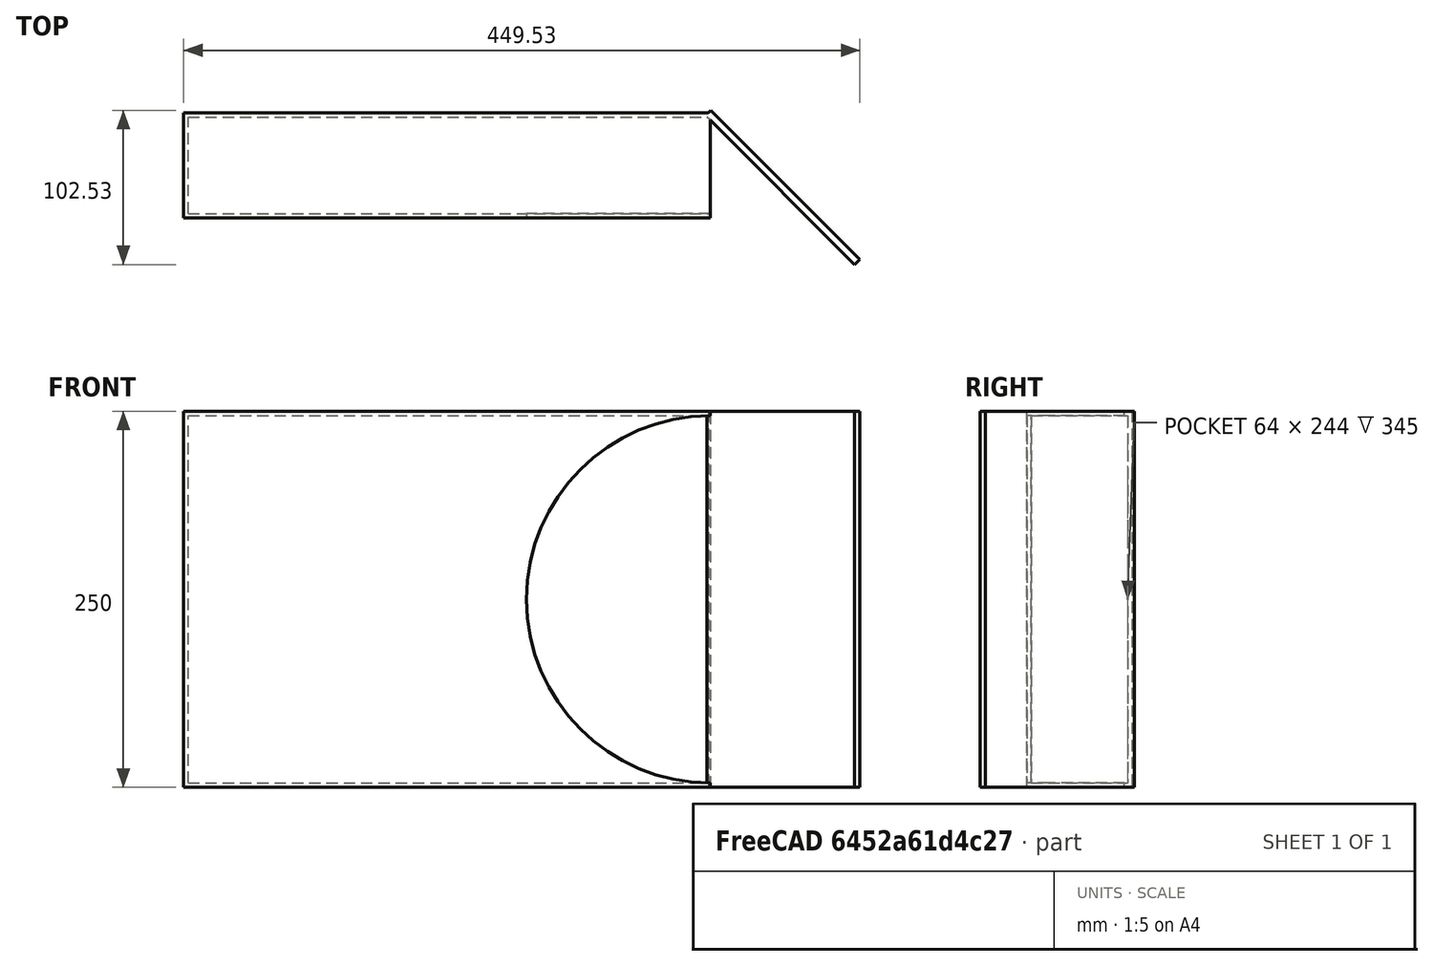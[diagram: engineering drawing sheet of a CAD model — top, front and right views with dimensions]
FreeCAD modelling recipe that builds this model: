
FCSTD DOCUMENT  (FreeCAD 0.16R6703 (Git))
Label: box
License: All rights reserved
LicenseURL: http://en.wikipedia.org/wiki/All_rights_reserved
objects: Part::Box×3, Part::Cut×2, Part::Cylinder×1, Part::MultiFuse×1
note: 7 computed .brp shape members not serialized (recipe doc carries the construction recipe); baked Part::Feature solids carry a one-line shape summary decoded from their .brp

FEATURE [Part::Box] Box  label="Cube"
  Height = 250
  Length = 350
  Placement = pos=(-175,-35,-125) rot=(0,0,1;0rad)
  Width = 70
FEATURE [Part::Box] Box001  label="Cube001"
  Height = 244
  Length = 350
  Placement = pos=(-172,-32,-122) rot=(0,0,1;0rad)
  Width = 64
FEATURE [Part::Cut] Cut
  Base = -> Box
  Tool = -> Box001
FEATURE [Part::Cylinder] Cylinder
  Angle = 360
  Height = 20
  Placement = pos=(175,-20,0) rot=(1,0,0;1.5708rad)
  Radius = 122
FEATURE [Part::Cut] Cut001
  Base = -> Cut
  Tool = -> Cylinder
FEATURE [Part::Box] Box002  label="Cube002"
  Height = 250
  Length = 140
  Placement = pos=(172,33,-125) rot=(0,0,-1;0.785398rad)
  Width = 5
FEATURE [Part::MultiFuse] Fusion
  Shapes = -> [Cut001,Box002]
